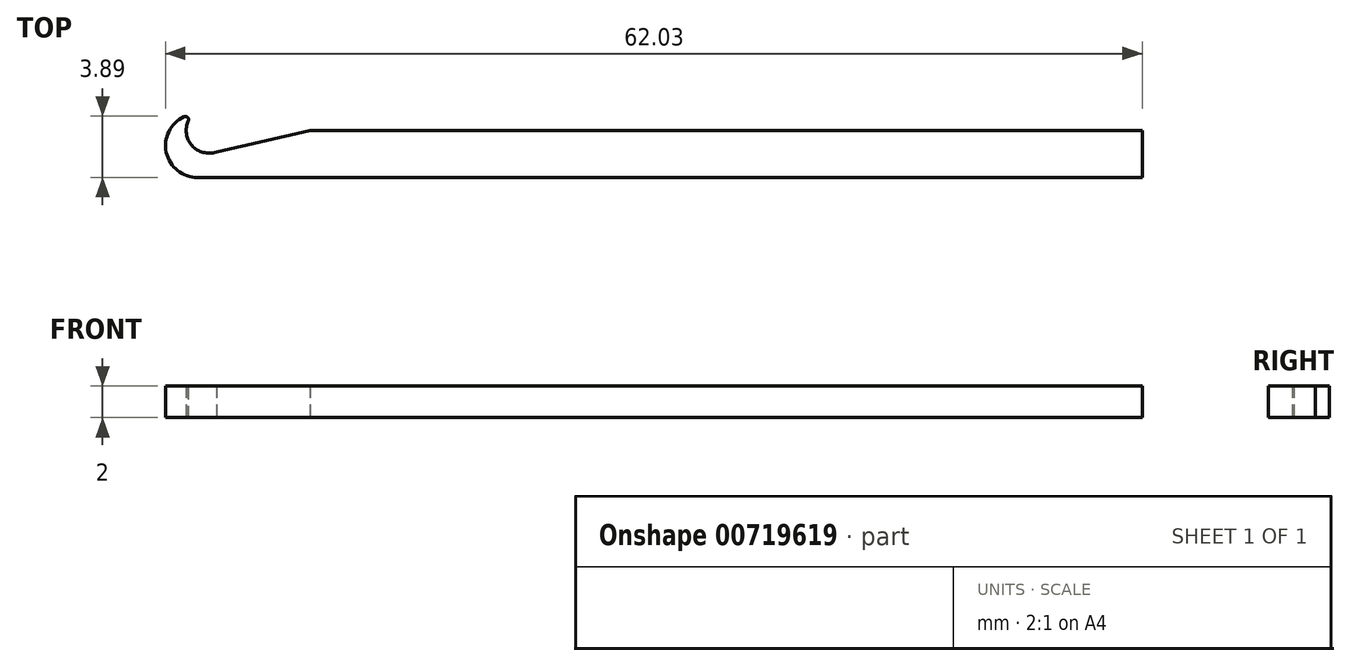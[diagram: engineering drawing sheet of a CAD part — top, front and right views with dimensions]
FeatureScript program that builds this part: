
annotation { "Feature Type Name" : "Feature", "Feature Type Description" : "" }
export const myFeature = defineFeature(function(context is Context, id is Id, definition is map)
    precondition{}
    {
        {
            var Q0;
            Q0=qCreatedBy(makeId("Top.planeOp"),FACE);
            var sketch = newSketch(context, id + "F0", { "sketchPlane" : qUnion([Q0])});
            skLineSegment(sketch, "E0.bottom", {"start": v(0, 0) * mm, "end": v(60, 0) * mm});
            skLineSegment(sketch, "E0.top", {"start": v(0, 3) * mm, "end": v(60, 3) * mm});
            skLineSegment(sketch, "E0.left", {"start": v(0, 0) * mm, "end": v(0, 3) * mm});
            skLineSegment(sketch, "E0.right", {"start": v(60, 0) * mm, "end": v(60, 3) * mm});
            skCircle(sketch, "E1", {"center": v(1.73, 3) * mm, "radius": 1 * mm});
            skCircle(sketch, "E2", {"center": v(0, 2.03) * mm, "radius": 2.03 * mm});
            skCircle(sketch, "E3", {"center": v(0.73, 3) * mm, "radius": 1.45 * mm});
            skLineSegment(sketch, "E4", {"start": v(0.92, 1.56) * mm, "end": v(7.13, 3) * mm});
            skSolve(sketch);
        }
        {
            var Q0;
            {var subQ2=sQuery(id+"F0.wireOp",EDGE,"E0.bottom");Q0=makeQuery(id+"F0.imprint","IMPRINT",FACE,{"disambiguationData":[TD([[makeQuery(id+"F0.imprint","IMPRINT",EDGE,{"derivedFrom":subQ2}),1.0]])]});}
            var Q1;
            {var subQ0=sQuery(id+"F0.wireOp",EDGE,"E4");var subQ1=sQuery(id+"F0.wireOp",EDGE,"E3");var subQ2=makeQuery(id+"F0.imprint","INTERSECT",VERTEX,{"disambiguationData":[OD(0.0)],"derivedFrom":[subQ1,subQ0]});Q1=makeQuery(id+"F0.imprint","IMPRINT",FACE,{"disambiguationData":[TD([[makeQuery(id+"F0.imprint","IMPRINT",EDGE,{"disambiguationData":[TD([[subQ2,1.0]])],"derivedFrom":subQ1}),-1.0]])]});}
            var Q2;
            {var subQ0=sQuery(id+"F0.wireOp",EDGE,"E2");var subQ3=sQuery(id+"F0.wireOp",EDGE,"E3");var subQ5=makeQuery(id+"F0.imprint","INTERSECT",VERTEX,{"disambiguationData":[OD(0.0)],"derivedFrom":[subQ0,subQ3]});Q2=makeQuery(id+"F0.imprint","IMPRINT",FACE,{"disambiguationData":[TD([[makeQuery(id+"F0.imprint","IMPRINT",EDGE,{"disambiguationData":[TD([[subQ5,-1.0]])],"derivedFrom":subQ3}),-1.0]])]});}
            extrude(context, id + "F1", {"entities" : qUnion([Q0, Q1, Q2]), "depth" : 2 * mm, "offsetDistance" : 25 * mm});
        }
        {
            var Q0;
            Q0=makeQuery(id+"F1.opExtrude","SWEPT_EDGE",EDGE,{"disambiguationData":[OSD([sQuery(id+"F0.wireOp",EDGE,"E2"),sQuery(id+"F0.wireOp",EDGE,"E3")])]});
            fillet(context, id + "F2", {"entities" : qUnion([Q0]), "radius" : .2 * mm, "tangentPropagation" : true, "allowEdgeOverflow" : false});
        }
    });
